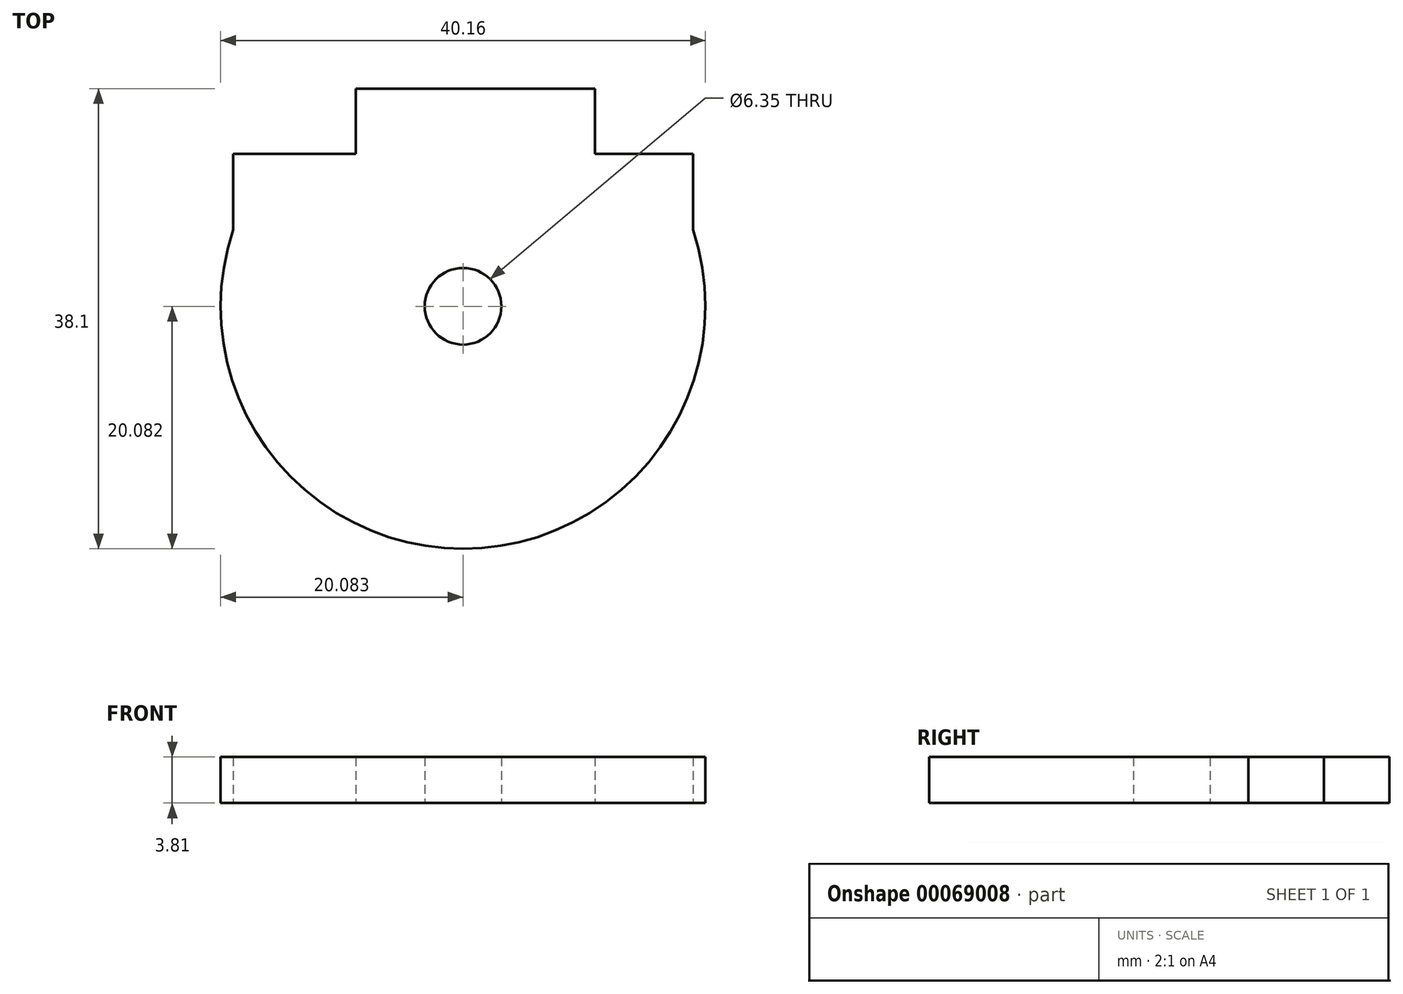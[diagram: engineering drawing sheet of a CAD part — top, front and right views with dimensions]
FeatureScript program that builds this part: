
annotation { "Feature Type Name" : "Feature", "Feature Type Description" : "" }
export const myFeature = defineFeature(function(context is Context, id is Id, definition is map)
    precondition{}
    {
        {
            var Q0;
            Q0=qCreatedBy(makeId("Top.planeOp"),FACE);
            var sketch = newSketch(context, id + "F0", { "sketchPlane" : qUnion([Q0])});
            skArc(sketch, "E0", {"start": v(-24.05, -22.32) * mm, "mid": v(-5, -48.75) * mm, "end": v(14.05, -22.32) * mm});
            skCircle(sketch, "E1", {"center": v(-5, -28.67) * mm, "radius": 3.18 * mm});
            skLineSegment(sketch, "E2", {"start": v(-24.05, -16.06) * mm, "end": v(-13.87, -16.06) * mm});
            skLineSegment(sketch, "E3", {"start": v(-13.87, -16.06) * mm, "end": v(-13.87, -10.65) * mm});
            skLineSegment(sketch, "E4", {"start": v(-13.87, -10.65) * mm, "end": v(5.94, -10.65) * mm});
            skLineSegment(sketch, "E5", {"start": v(5.94, -10.65) * mm, "end": v(5.94, -16.06) * mm});
            skLineSegment(sketch, "E6", {"start": v(5.94, -16.06) * mm, "end": v(14.05, -16.06) * mm});
            skLineSegment(sketch, "E7", {"start": v(-24.05, -16.06) * mm, "end": v(-24.05, -22.32) * mm});
            skLineSegment(sketch, "E8", {"start": v(14.05, -16.06) * mm, "end": v(14.05, -22.32) * mm});
            skSolve(sketch);
        }
        {
            var Q0;
            Q0=makeQuery(id+"F0.imprint","IMPRINT",FACE,{"disambiguationData":[TD([[makeQuery(id+"F0.imprint","IMPRINT",EDGE,{"derivedFrom":sQuery(id+"F0.wireOp",EDGE,"E0")}),1.0]])]});
            extrude(context, id + "F1", {"entities" : qUnion([Q0]), "depth" : 3.8 * mm});
        }
    });
